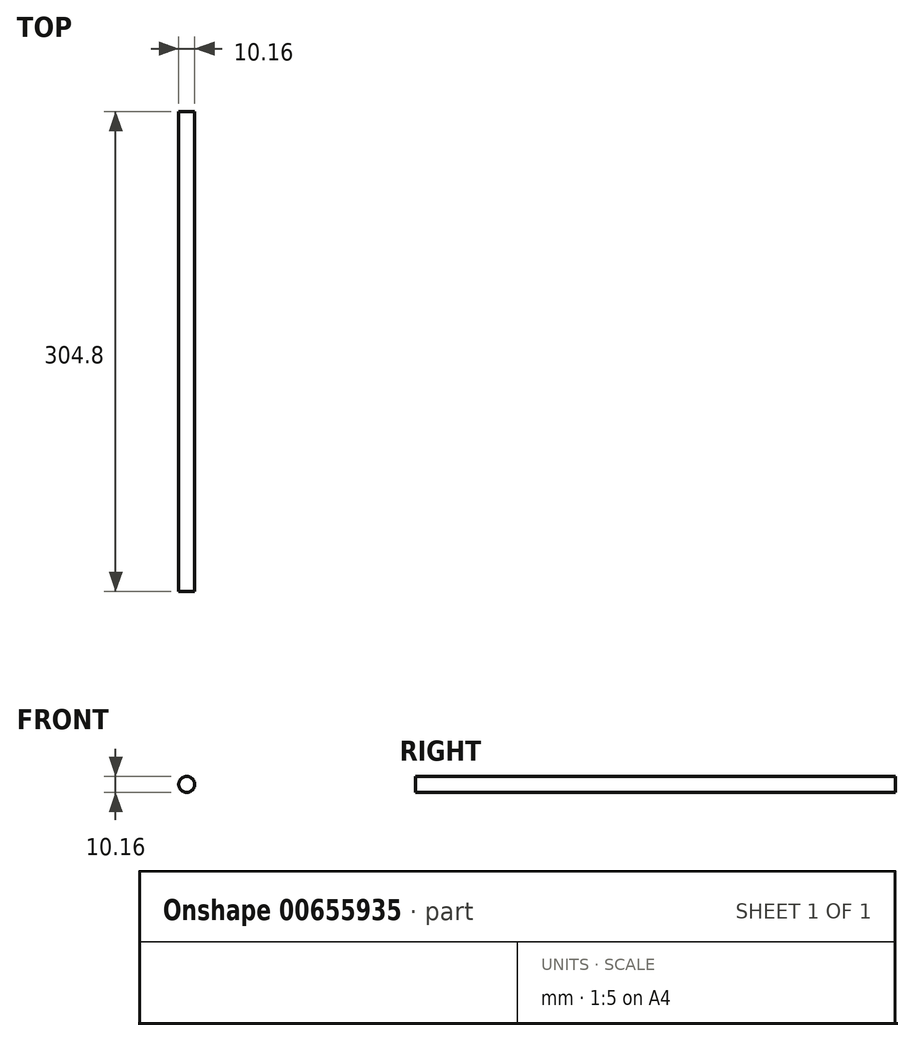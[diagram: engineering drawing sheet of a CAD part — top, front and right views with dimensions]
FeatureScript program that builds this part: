
annotation { "Feature Type Name" : "Feature", "Feature Type Description" : "" }
export const myFeature = defineFeature(function(context is Context, id is Id, definition is map)
    precondition{}
    {
        {
            var Q0;
            Q0=qCreatedBy(makeId("Front.planeOp"),FACE);
            var sketch = newSketch(context, id + "F0", { "sketchPlane" : qUnion([Q0])});
            skCircle(sketch, "E0", {"center": v(0, 0) * mm, "radius": 5.08 * mm});
            skSolve(sketch);
        }
        {
            var Q0;
            Q0=qSketchRegion(id+"F0",true);
            extrude(context, id + "F1", {"entities" : qUnion([Q0]), "depth" : 304.8 * mm, "offsetDistance" : 25.4 * mm});
        }
    });
